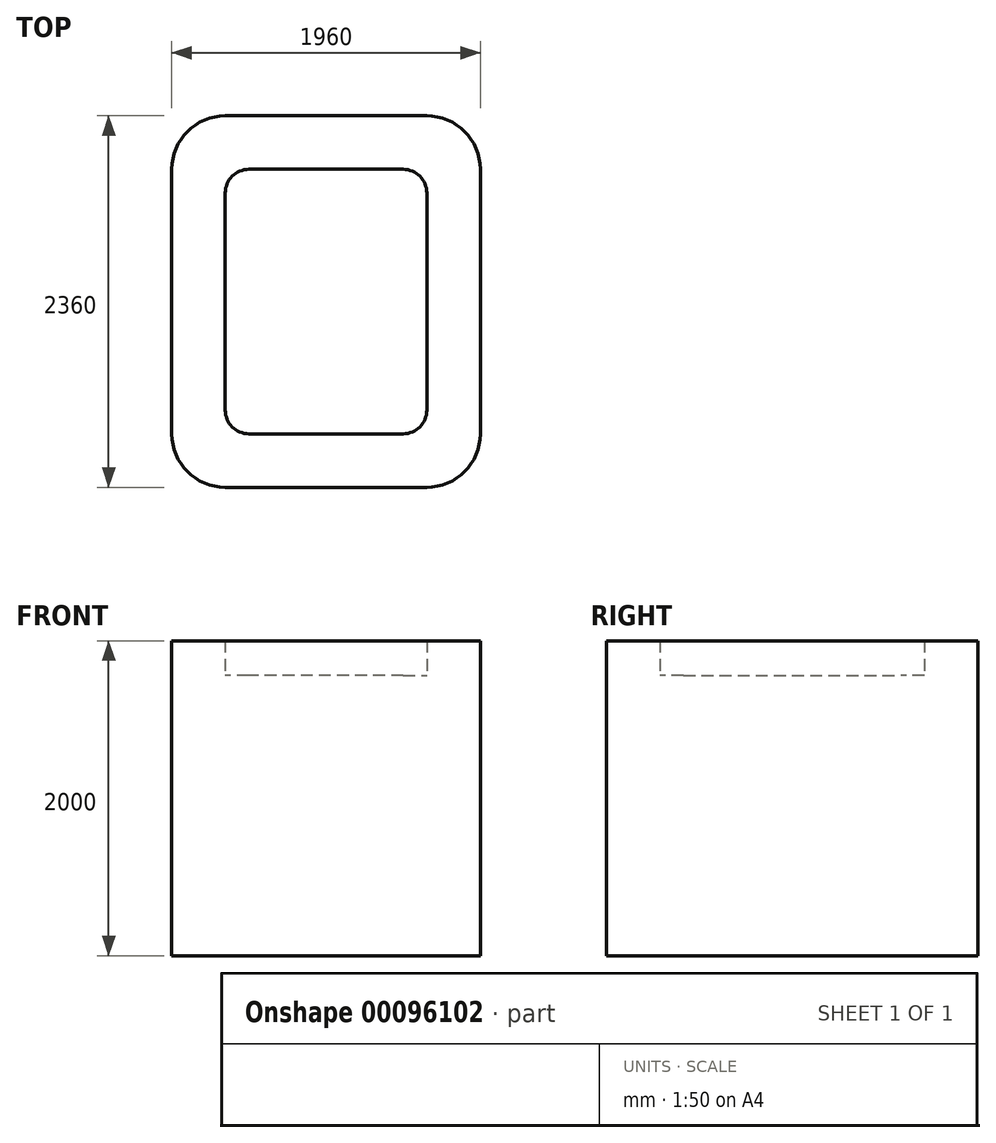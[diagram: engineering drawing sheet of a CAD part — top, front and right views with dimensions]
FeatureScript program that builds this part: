
annotation { "Feature Type Name" : "Feature", "Feature Type Description" : "" }
export const myFeature = defineFeature(function(context is Context, id is Id, definition is map)
    precondition{}
    {
        {
            var Q0;
            Q0=qCreatedBy(makeId("Top.planeOp"),FACE);
            var sketch = newSketch(context, id + "F0", { "sketchPlane" : qUnion([Q0])});
            skLineSegment(sketch, "E0.bottom", {"start": v(980, -1180) * mm, "end": v(-980, -1180) * mm});
            skLineSegment(sketch, "E0.top", {"start": v(980, 1180) * mm, "end": v(-980, 1180) * mm});
            skLineSegment(sketch, "E0.left", {"start": v(980, -1180) * mm, "end": v(980, 1180) * mm});
            skLineSegment(sketch, "E0.right", {"start": v(-980, -1180) * mm, "end": v(-980, 1180) * mm});
            skPoint(sketch, "E0.middle", {"position": v(0, 0) * mm});
            skSolve(sketch);
        }
        {
            var Q0;
            Q0=qSketchRegion(id+"F0",true);
            var Q1;
            Q1=makeQuery(id+"F0.imprint","IMPRINT",FACE,{"disambiguationData":[TD([[makeQuery(id+"F0.imprint","IMPRINT",EDGE,{"derivedFrom":sQuery(id+"F0.wireOp",EDGE,"E0.bottom")}),-1.0]])]});
            extrude(context, id + "F1", {"entities" : qUnion([Q0, Q1]), "depth" : 560 * mm});
        }
        {
            var Q0;
            Q0=makeQuery(id+"F1.opExtrude","CAP_FACE",FACE,{"disambiguationData":[OSD([sQuery(id+"F0.wireOp",EDGE,"E0.bottom"),sQuery(id+"F0.wireOp",EDGE,"E0.top"),sQuery(id+"F0.wireOp",EDGE,"E0.left"),sQuery(id+"F0.wireOp",EDGE,"E0.right")])],"isStart":false});
            shell(context, id + "F2", {"entities" : qUnion([Q0]), "thickness" : 340 * mm});
        }
        {
            var Q0;
            Q0=makeQuery(id+"F1.opExtrude","SWEPT_EDGE",EDGE,{"disambiguationData":[OSD([sQuery(id+"F0.wireOp",EDGE,"E0.top"),sQuery(id+"F0.wireOp",EDGE,"E0.right")])]});
            var Q1;
            Q1=makeQuery(id+"F1.opExtrude","SWEPT_EDGE",EDGE,{"disambiguationData":[OSD([sQuery(id+"F0.wireOp",EDGE,"E0.top"),sQuery(id+"F0.wireOp",EDGE,"E0.left")])]});
            var Q2;
            Q2=makeQuery(id+"F1.opExtrude","SWEPT_EDGE",EDGE,{"disambiguationData":[OSD([sQuery(id+"F0.wireOp",EDGE,"E0.bottom"),sQuery(id+"F0.wireOp",EDGE,"E0.right")])]});
            var Q3;
            Q3=makeQuery(id+"F1.opExtrude","SWEPT_EDGE",EDGE,{"disambiguationData":[OSD([sQuery(id+"F0.wireOp",EDGE,"E0.bottom"),sQuery(id+"F0.wireOp",EDGE,"E0.left")])]});
            fillet(context, id + "F3", {"entities" : qUnion([Q0, Q1, Q2, Q3]), "radius" : 340 * mm, "tangentPropagation" : true, "allowEdgeOverflow" : false});
        }
        {
            var Q0;
            Q0=makeQuery(id+"F2.opShell","OFFSET_EDGE",EDGE,{"disambiguationData":[OSD([sQuery(id+"F0.wireOp",EDGE,"E0.top"),sQuery(id+"F0.wireOp",EDGE,"E0.left")])]});
            var Q1;
            Q1=makeQuery(id+"F2.opShell","OFFSET_EDGE",EDGE,{"disambiguationData":[OSD([sQuery(id+"F0.wireOp",EDGE,"E0.bottom"),sQuery(id+"F0.wireOp",EDGE,"E0.left")])]});
            var Q2;
            Q2=makeQuery(id+"F2.opShell","OFFSET_EDGE",EDGE,{"disambiguationData":[OSD([sQuery(id+"F0.wireOp",EDGE,"E0.bottom"),sQuery(id+"F0.wireOp",EDGE,"E0.right")])]});
            var Q3;
            Q3=makeQuery(id+"F2.opShell","OFFSET_EDGE",EDGE,{"disambiguationData":[OSD([sQuery(id+"F0.wireOp",EDGE,"E0.top"),sQuery(id+"F0.wireOp",EDGE,"E0.right")])]});
            fillet(context, id + "F4", {"entities" : qUnion([Q0, Q1, Q2, Q3]), "radius" : 150 * mm, "tangentPropagation" : true, "allowEdgeOverflow" : false});
        }
        {
            var Q0;
            Q0=makeQuery(id+"F1.opExtrude","CAP_FACE",FACE,{"disambiguationData":[OSD([sQuery(id+"F0.wireOp",EDGE,"E0.bottom"),sQuery(id+"F0.wireOp",EDGE,"E0.top"),sQuery(id+"F0.wireOp",EDGE,"E0.left"),sQuery(id+"F0.wireOp",EDGE,"E0.right")])],"isStart":true});
            extrude(context, id + "F5", {"entities" : qUnion([Q0]), "operationType" : NewBodyOperationType.ADD, "depth" : 1440 * mm});
        }
    });
